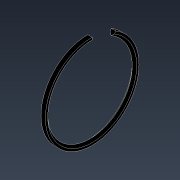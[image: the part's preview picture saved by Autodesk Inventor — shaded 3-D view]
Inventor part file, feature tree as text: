
AUTODESK INVENTOR PART (.ipt)
format: ipt  version: 2022 (Build 260153000, 153)  size: 96,768 bytes
history: native  units: mm
features: revolve x1, sketch x1
ambient origin geometry x8: Origin, YZ Plane, XZ Plane, XY Plane, X Axis, Y Axis, Z Axis, Center Point
bodies: Solid1 (feature_tree)
feature tree (2):
  revolve  "Revolution1"  [1 undecoded]
  sketch  "Sketch1"  dims[d0=2.0mm d1=10.0mm d3=57.0mm d4=2.828mm d5=1.5mm d6=330.0deg]
note: 1 required parameter value undecoded (feature->parameter linkage not recoverable at this tier; creation-order binding heuristic only, values carry confidence <= 0.55)
